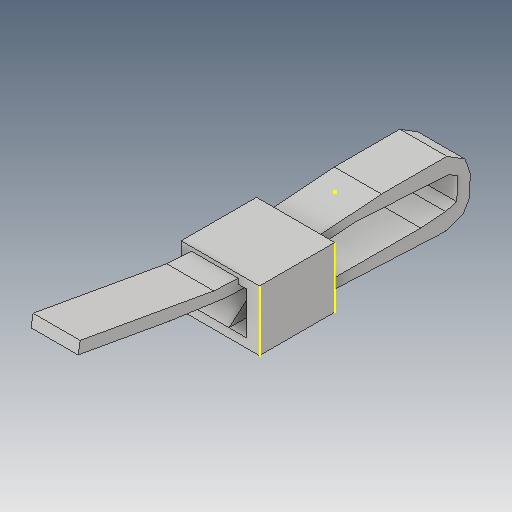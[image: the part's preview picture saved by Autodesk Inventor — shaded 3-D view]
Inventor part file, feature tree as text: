
AUTODESK INVENTOR PART (.ipt)
format: ipt  version: 2017 (Build 210142000, 142)  size: 147,456 bytes
history: native  units: mm
features: sketch x4, extrude x3
ambient origin geometry x8: Origin, YZ Plane, XZ Plane, XY Plane, X Axis, Y Axis, Z Axis, Center Point
bodies: Solid1 (feature_tree)
feature tree (7):
  extrude  "Extrusion1"  Depth=2.5mm TaperAngle=0.0deg
  sketch  "Sketch3"  dims[d4=2.0mm d5=0.0mm]
  extrude  "Extrusion2"  [1 undecoded]
  extrude  "Extrusion3"  [1 undecoded]
  sketch  "Sketch1"  dims[d0=4.0mm d1=0.0mm d2=2.5mm d3=0.0mm]
  sketch  "Sketch4"
  sketch  "Sketch5"
note: 2 required parameter values undecoded (feature->parameter linkage not recoverable at this tier; creation-order binding heuristic only, values carry confidence <= 0.55)
